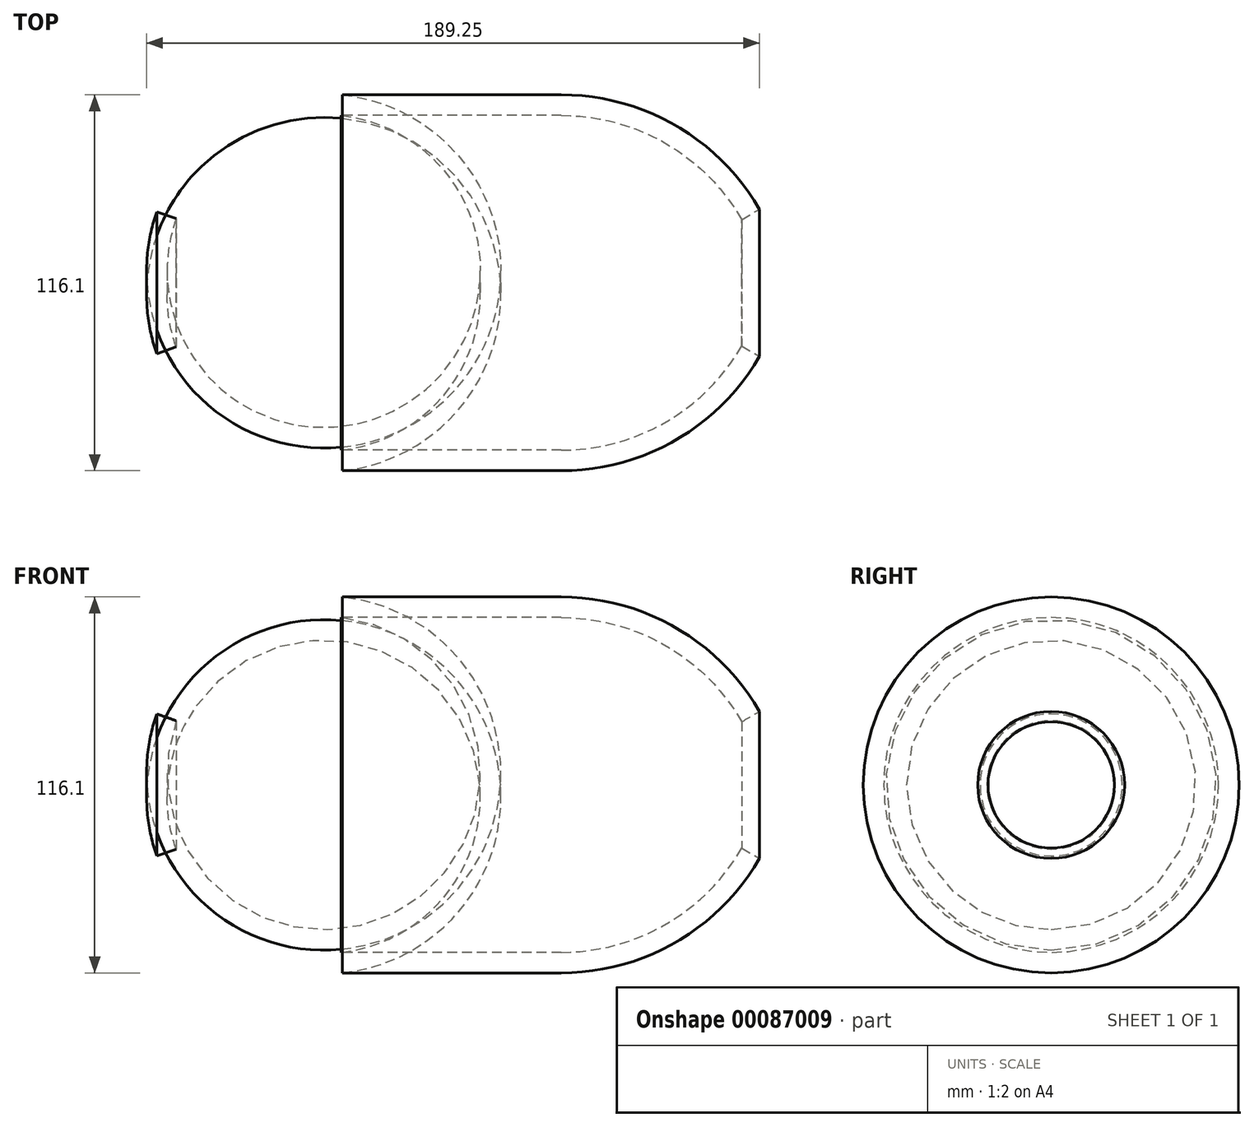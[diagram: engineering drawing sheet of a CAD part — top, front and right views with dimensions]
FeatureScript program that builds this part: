
annotation { "Feature Type Name" : "Feature", "Feature Type Description" : "" }
export const myFeature = defineFeature(function(context is Context, id is Id, definition is map)
    precondition{}
    {
        {
            var Q0;
            Q0=qCreatedBy(makeId("Top.planeOp"),FACE);
            var sketch = newSketch(context, id + "F0", { "sketchPlane" : qUnion([Q0])});
            skArc(sketch, "E0", {"start": v(-38.14, 51.7) * mm, "mid": v(-69.18, 44.64) * mm, "end": v(-89.1, 19.82) * mm});
            skLineSegment(sketch, "E1", {"start": v(-38.14, 51.7) * mm, "end": v(29.8, 51.7) * mm});
            skArc(sketch, "E2", {"start": v(85.52, 19.52) * mm, "mid": v(61.97, 43.08) * mm, "end": v(29.8, 51.7) * mm});
            skArc(sketch, "E3.0", {"start": v(-37.43, 58.01) * mm, "mid": v(-72.55, 50.02) * mm, "end": v(-95.08, 21.94) * mm});
            skLineSegment(sketch, "E4.0", {"start": v(-38.14, 58.05) * mm, "end": v(29.8, 58.05) * mm});
            skArc(sketch, "E5.0", {"start": v(91.02, 22.7) * mm, "mid": v(65.15, 48.58) * mm, "end": v(29.8, 58.05) * mm});
            skLineSegment(sketch, "E6", {"start": v(-95.08, 21.94) * mm, "end": v(-89.1, 19.82) * mm});
            skLineSegment(sketch, "E7", {"start": v(85.52, 19.52) * mm, "end": v(91.02, 22.7) * mm});
            skLineSegment(sketch, "E8", {"start": v(-42.02, 0) * mm, "end": v(32.78, 0) * mm});
            skSolve(sketch);
        }
        {
            var Q0;
            Q0 = qSketchRegion(id + "F0", true);
            var Q1;
            Q1=sQuery(id+"F0.wireOp",EDGE,"E8");
            revolve(context, id + "F1", {"entities" : qUnion([Q0]), "axis" : qUnion([Q1]), "revolveType" : RevolveType.FULL});
        }
    });
